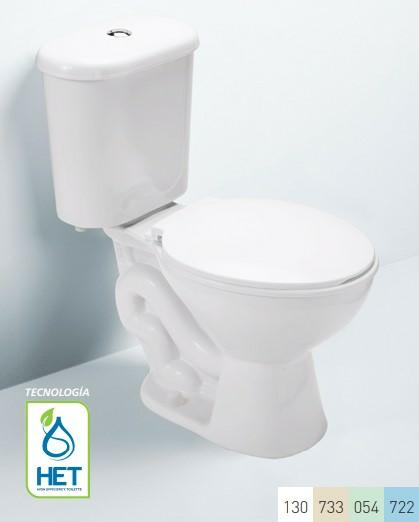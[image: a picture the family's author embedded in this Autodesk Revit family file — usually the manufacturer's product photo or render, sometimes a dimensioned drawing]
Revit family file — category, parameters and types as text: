
# Revit family: BRG-GRF-LVM_BELA MONOMANDO COCINA ESTÁNDAR CROMO v_02
name_source: partatom
category: Aparatos sanitarios
units: mm (PartAtom-declared; Revit-internal decimal feet)

## family parameters
Compartido = Sí
Corte con vacíos al cargar = No
Cota de conector redondo = Diámetro de uso
Número OmniClass = 23.45.00.00
Punto de cálculo de habitación = Sí
Se basa en plano de trabajo = No
Siempre vertical = Sí
Tipo de pieza = Normal
Título OmniClass = Sanitary, Laundry, and Cleaning Equipment

## types (1)
- BELA MONOMANDO PARA COCINA
    Conexión AC = Sí
    Conexión AF = Sí
    Conexión de residuos = Sí
    Conexión de ventilación = Sí
    Fabricante = BRIGGS Ecuador
    Imagen de tipo = <Ninguno>
    Modelo = BELA MONOMANDO PARA COCINA
    URL = https://www.briggs.com.ec
    _ALT_Basamento = 0.85 m
    _ALT_Eje instalación = 0.6 m
    _EDESA_ Alto en cm = 35.4
    _EDESA_ Ancho en cm = 9.2
    _EDESA_ Categoría = Productos > Grifería > Cocina
    _EDESA_ Certificación = Cumple con norma NTE - INEN 3123 basada en la norma ASME 112.18.1 - 2012. Nuestras mangueras cuentan certificación cUPC.
    _EDESA_ Color = Cromo
    _EDESA_ Conexión hidráulica = Entrada de agua: tubería ø 1/2" Salida de agua: tubería PVC 50
    _EDESA_ Consumo/capacidad de agua en L = 8.3 litros por minuto / 2.2 gpm a 60 psi
    _EDESA_ Descripción = Grifería monomando de cocina para agua fría y caliente. Instalación sobre fregadero o mesón. Incluye mangueras flexibles.
    _EDESA_ Garantía = De por vida para el cuerpo principal y acabado en cromo (306)
    _EDESA_ Manual de instalación = https://www.briggs.com.ec
    _EDESA_ Marca = BRIGGS
    _EDESA_ Materiales = Latón
    _EDESA_ Nombre = BELA MONOMANDO PARA COCINA
    _EDESA_ Productos incluídos = 2 Mangueras monomando 16"
    _EDESA_ Productos necesarios para instalación = Desagüe y Sifón para fregadero
    _EDESA_ Profundidad en cm = 21
    _EDESA_ Sku/código = SG0087083061CW
    _EDESA_ Tipo de instalación = Sobre fregadero o mesón
